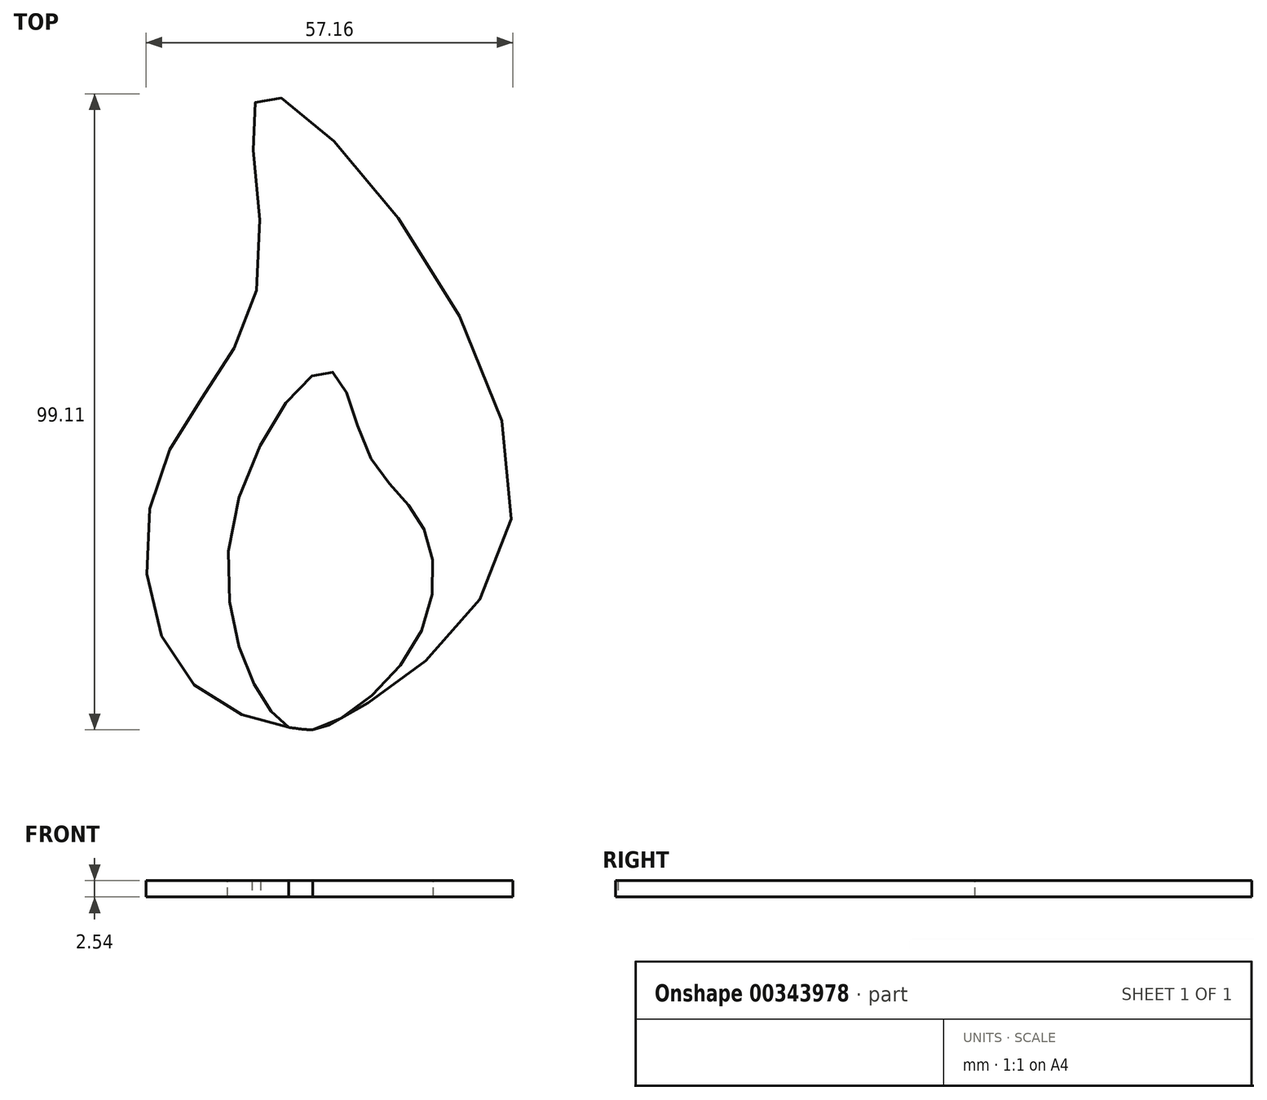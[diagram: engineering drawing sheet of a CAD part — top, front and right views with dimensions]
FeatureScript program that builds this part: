
annotation { "Feature Type Name" : "Feature", "Feature Type Description" : "" }
export const myFeature = defineFeature(function(context is Context, id is Id, definition is map)
    precondition{}
    {
        {
            var Q0;
            Q0=qCreatedBy(makeId("Top.planeOp"),FACE);
            var sketch = newSketch(context, id + "F0", { "sketchPlane" : qUnion([Q0])});
            skFitSpline(sketch, "E0", {"points": [v(-2.5, -46.61) * mm, v(0, -45.89) * mm, v(28.6, -12) * mm, v(-10, 52.48) * mm, v(-10.94, 23.77) * mm, v(-26.47, -6.82) * mm, v(-20.83, -39.77) * mm, v(-2.5, -46.61) * mm]});
            skFitSpline(sketch, "E1", {"points": [v(-2.5, -46.61) * mm, v(-9.25, -43.42) * mm, v(-15.14, -15.2) * mm, v(0, 9.36) * mm, v(6.14, -3.5) * mm, v(14.52, -14.65) * mm, v(13.77, -32.6) * mm, v(-2.5, -46.61) * mm]});
            skSolve(sketch);
        }
        {
            var Q0;
            {var subQ0=sQuery(id+"F0.wireOp",EDGE,"E1");var subQ1=sQuery(id+"F0.wireOp",EDGE,"E0");var subQ2=makeQuery(id+"F0.imprint","INTERSECT",VERTEX,{"disambiguationData":[OD(0.0)],"derivedFrom":[subQ1,subQ0]});Q0=makeQuery(id+"F0.imprint","IMPRINT",FACE,{"disambiguationData":[TD([[makeQuery(id+"F0.imprint","IMPRINT",EDGE,{"disambiguationData":[TD([[subQ2,1.0]])],"derivedFrom":subQ1}),1.0]])]});}
            extrude(context, id + "F1", {"entities" : qUnion([Q0]), "depth" : 2.54 * mm});
        }
        {
            var Q0;
            {var subQ0=sQuery(id+"F0.wireOp",EDGE,"E1");var subQ1=sQuery(id+"F0.wireOp",EDGE,"E0");var subQ2=makeQuery(id+"F0.imprint","INTERSECT",VERTEX,{"disambiguationData":[OD(0.0)],"derivedFrom":[subQ1,subQ0]});Q0=makeQuery(id+"F0.imprint","IMPRINT",FACE,{"disambiguationData":[TD([[makeQuery(id+"F0.imprint","IMPRINT",EDGE,{"disambiguationData":[TD([[subQ2,-1.0]])],"derivedFrom":subQ1}),1.0]])]});}
            extrude(context, id + "F2", {"entities" : qUnion([Q0]), "depth" : 2.54 * mm});
        }
    });
